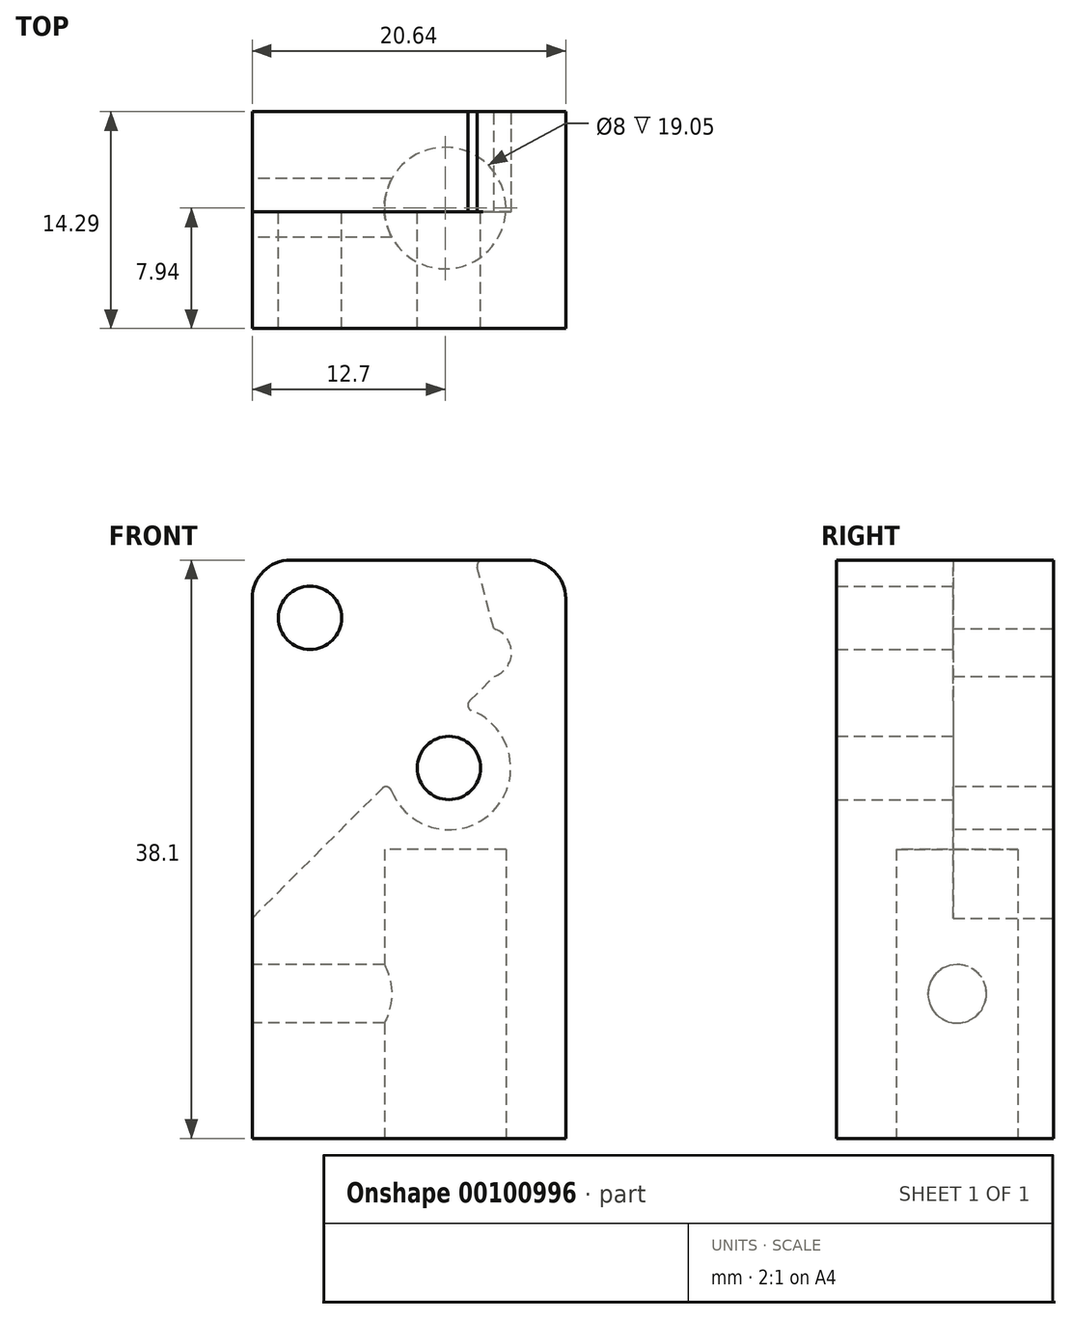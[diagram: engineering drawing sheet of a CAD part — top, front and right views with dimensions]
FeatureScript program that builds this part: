
annotation { "Feature Type Name" : "Feature", "Feature Type Description" : "" }
export const myFeature = defineFeature(function(context is Context, id is Id, definition is map)
    precondition{}
    {
        {
            var Q0;
            Q0=qCreatedBy(makeId("Top.planeOp"),FACE);
            var sketch = newSketch(context, id + "F0", { "sketchPlane" : qUnion([Q0])});
            skLineSegment(sketch, "E0.bottom", {"start": v(7.94, 6.35) * mm, "end": v(-12.7, 6.35) * mm});
            skLineSegment(sketch, "E0.top", {"start": v(7.94, -7.94) * mm, "end": v(-12.7, -7.94) * mm});
            skLineSegment(sketch, "E0.left", {"start": v(7.94, 6.35) * mm, "end": v(7.94, -7.94) * mm});
            skLineSegment(sketch, "E0.right", {"start": v(-12.7, 6.35) * mm, "end": v(-12.7, -7.94) * mm});
            skPoint(sketch, "E0.middle", {"position": v(-4.76, 0) * mm});
            skSolve(sketch);
        }
        {
            var Q0;
            Q0 = qSketchRegion(id + "F0", true);
            extrude(context, id + "F1", {"entities" : qUnion([Q0]), "depth" : 38.1 * mm});
        }
        {
            var Q0;
            Q0=qCreatedBy(makeId("Top.planeOp"),FACE);
            var sketch = newSketch(context, id + "F2", { "sketchPlane" : qUnion([Q0])});
            skCircle(sketch, "E1", {"center": v(0, 0) * mm, "radius": 4 * mm});
            skSolve(sketch);
        }
        {
            var Q0;
            Q0 = qSketchRegion(id + "F2", true);
            extrude(context, id + "F3", {"entities" : qUnion([Q0]), "operationType" : NewBodyOperationType.REMOVE, "depth" : 19.05 * mm});
        }
        {
            var Q0;
            Q0=qCreatedBy(makeId("Front.planeOp"),FACE);
            cPlane(context, id + "F4", {"entities" : qUnion([Q0]), "cplaneType" : CPlaneType.OFFSET, "offset" : 0.25 * mm, "width" : 152.4 * mm, "height" : 152.4 * mm});
        }
        {
            var Q0;
            Q0=qCreatedBy(id+"F4.planeOp",FACE);
            var sketch = newSketch(context, id + "F5", { "sketchPlane" : qUnion([Q0])});
            skLineSegment(sketch, "E2", {"start": v(-24.26, 2.94) * mm, "end": v(3.88, 31.08) * mm});
            skLineSegment(sketch, "E3", {"start": v(3.88, 31.08) * mm, "end": v(1.14, 41.27) * mm});
            skLineSegment(sketch, "E4", {"start": v(1.14, 41.27) * mm, "end": v(-24.26, 41.27) * mm});
            skLineSegment(sketch, "E5", {"start": v(-24.26, 41.27) * mm, "end": v(-24.26, 2.94) * mm});
            skLineSegment(sketch, "E6", {"start": v(1.14, 41.27) * mm, "end": v(-24.26, 15.87) * mm, "construction": true});
            skSolve(sketch);
        }
        {
            var Q0;
            Q0 = qSketchRegion(id + "F5", true);
            extrude(context, id + "F6", {"entities" : qUnion([Q0]), "operationType" : NewBodyOperationType.REMOVE, "oppositeDirection" : true, "depth" : 22.62 * mm});
        }
        {
            var Q0;
            Q0=makeQuery(id+"F1.opExtrude","SWEPT_FACE",FACE,{"disambiguationData":[OSD([sQuery(id+"F0.wireOp",EDGE,"E0.bottom")])]});
            var sketch = newSketch(context, id + "F7", { "sketchPlane" : qUnion([Q0])});
            skCircle(sketch, "E7", {"center": v(-2.72, 32) * mm, "radius": 1.65 * mm});
            skLineSegment(sketch, "E8", {"start": v(-3.88, 31.08) * mm, "end": v(-2.72, 32) * mm, "construction": true});
            skSolve(sketch);
        }
        {
            var Q0;
            Q0 = qSketchRegion(id + "F7", true);
            var Q1;
            Q1=makeQuery(id+"F6.boolean.opBoolean","COPY",FACE,{"derivedFrom":makeQuery(id+"F6.opExtrude","CAP_FACE",FACE,{"disambiguationData":[OSD([sQuery(id+"F5.wireOp",EDGE,"E2"),sQuery(id+"F5.wireOp",EDGE,"E3"),sQuery(id+"F5.wireOp",EDGE,"E4"),sQuery(id+"F5.wireOp",EDGE,"E5")])],"isStart":true})});
            extrude(context, id + "F8", {"entities" : qUnion([Q0]), "operationType" : NewBodyOperationType.REMOVE, "endBound" : BoundingType.UP_TO_SURFACE, "oppositeDirection" : true, "endBoundEntityFace" : qUnion([Q1]), "depth" : 25.4 * mm});
        }
        {
            var Q0;
            Q0=makeQuery(id+"F1.opExtrude","SWEPT_FACE",FACE,{"disambiguationData":[OSD([sQuery(id+"F0.wireOp",EDGE,"E0.bottom")])]});
            var sketch = newSketch(context, id + "F9", { "sketchPlane" : qUnion([Q0])});
            skCircle(sketch, "E9", {"center": v(-0.25, 24.4) * mm, "radius": 2.16 * mm, "construction": true});
            skCircle(sketch, "E10", {"center": v(8.9, 34.3) * mm, "radius": 2.16 * mm, "construction": true});
            skCircle(sketch, "E11", {"center": v(-0.25, 24.4) * mm, "radius": 2.08 * mm});
            skCircle(sketch, "E12", {"center": v(8.9, 34.3) * mm, "radius": 2.08 * mm});
            skSolve(sketch);
        }
        {
            var Q0;
            Q0 = qSketchRegion(id + "F9", true);
            extrude(context, id + "F10", {"entities" : qUnion([Q0]), "operationType" : NewBodyOperationType.REMOVE, "oppositeDirection" : true, "depth" : 25.4 * mm});
        }
        {
            var Q0;
            Q0=makeQuery(id+"F8.boolean.opBoolean","MERGE",FACE,{"derivedFrom":[makeQuery(id+"F6.boolean.opBoolean","COPY",FACE,{"derivedFrom":makeQuery(id+"F6.opExtrude","CAP_FACE",FACE,{"disambiguationData":[OSD([sQuery(id+"F5.wireOp",EDGE,"E2"),sQuery(id+"F5.wireOp",EDGE,"E3"),sQuery(id+"F5.wireOp",EDGE,"E4"),sQuery(id+"F5.wireOp",EDGE,"E5")])],"isStart":true})}),makeQuery(id+"F8.opExtrude","CAP_FACE",FACE,{"disambiguationData":[OSD([sQuery(id+"F7.wireOp",EDGE,"E7")])],"isStart":false})]});
            var sketch = newSketch(context, id + "F11", { "sketchPlane" : qUnion([Q0])});
            skCircle(sketch, "E13", {"center": v(-0.25, 24.4) * mm, "radius": 4.06 * mm});
            skSolve(sketch);
        }
        {
            var Q0;
            Q0 = qSketchRegion(id + "F11", true);
            extrude(context, id + "F12", {"entities" : qUnion([Q0]), "operationType" : NewBodyOperationType.REMOVE, "depth" : 25.4 * mm});
        }
        {
            var Q0;
            Q0=makeQuery(id+"F12.boolean.opBoolean","INTERSECT",EDGE,{"disambiguationData":[OD(0.0)],"derivedFrom":[makeQuery(id+"F6.boolean.opBoolean","COPY",FACE,{"derivedFrom":makeQuery(id+"F6.opExtrude","SWEPT_FACE",FACE,{"disambiguationData":[OSD([sQuery(id+"F5.wireOp",EDGE,"E2")])]})}),makeQuery(id+"F12.opExtrude","SWEPT_FACE",FACE,{"disambiguationData":[OSD([sQuery(id+"F11.wireOp",EDGE,"E13")])]})]});
            var Q1;
            Q1=makeQuery(id+"F12.boolean.opBoolean","INTERSECT",EDGE,{"disambiguationData":[OD(1.0)],"derivedFrom":[makeQuery(id+"F6.boolean.opBoolean","COPY",FACE,{"derivedFrom":makeQuery(id+"F6.opExtrude","SWEPT_FACE",FACE,{"disambiguationData":[OSD([sQuery(id+"F5.wireOp",EDGE,"E2")])]})}),makeQuery(id+"F12.opExtrude","SWEPT_FACE",FACE,{"disambiguationData":[OSD([sQuery(id+"F11.wireOp",EDGE,"E13")])]})]});
            var Q2;
            Q2=makeQuery(id+"F6.boolean.opBoolean","INTERSECT",EDGE,{"derivedFrom":[makeQuery(id+"F1.opExtrude","CAP_FACE",FACE,{"disambiguationData":[OSD([sQuery(id+"F0.wireOp",EDGE,"E0.bottom"),sQuery(id+"F0.wireOp",EDGE,"E0.top"),sQuery(id+"F0.wireOp",EDGE,"E0.left"),sQuery(id+"F0.wireOp",EDGE,"E0.right")])],"isStart":false}),makeQuery(id+"F6.opExtrude","SWEPT_FACE",FACE,{"disambiguationData":[OSD([sQuery(id+"F5.wireOp",EDGE,"E3")])]})]});
            fillet(context, id + "F13", {"entities" : qUnion([Q0, Q1, Q2]), "radius" : 0.38 * mm, "tangentPropagation" : true, "allowEdgeOverflow" : false});
        }
        {
            var Q0;
            Q0=makeQuery(id+"F1.opExtrude","SWEPT_FACE",FACE,{"disambiguationData":[OSD([sQuery(id+"F0.wireOp",EDGE,"E0.right")])]});
            var sketch = newSketch(context, id + "F14", { "sketchPlane" : qUnion([Q0])});
            skCircle(sketch, "E14", {"center": v(0, 9.53) * mm, "radius": 1.93 * mm});
            skSolve(sketch);
        }
        {
            var Q0;
            Q0 = qSketchRegion(id + "F14", true);
            extrude(context, id + "F15", {"entities" : qUnion([Q0]), "operationType" : NewBodyOperationType.REMOVE, "oppositeDirection" : true, "depth" : 15.32 * mm});
        }
        {
            var Q0;
            Q0=makeQuery(id+"F1.opExtrude","CAP_EDGE",EDGE,{"disambiguationData":[OSD([sQuery(id+"F0.wireOp",EDGE,"E0.right")])],"isStart":false});
            var Q1;
            Q1=makeQuery(id+"F1.opExtrude","CAP_EDGE",EDGE,{"disambiguationData":[OSD([sQuery(id+"F0.wireOp",EDGE,"E0.left")])],"isStart":false});
            fillet(context, id + "F16", {"entities" : qUnion([Q0, Q1]), "radius" : 2.54 * mm, "tangentPropagation" : true, "allowEdgeOverflow" : false});
        }
    });
